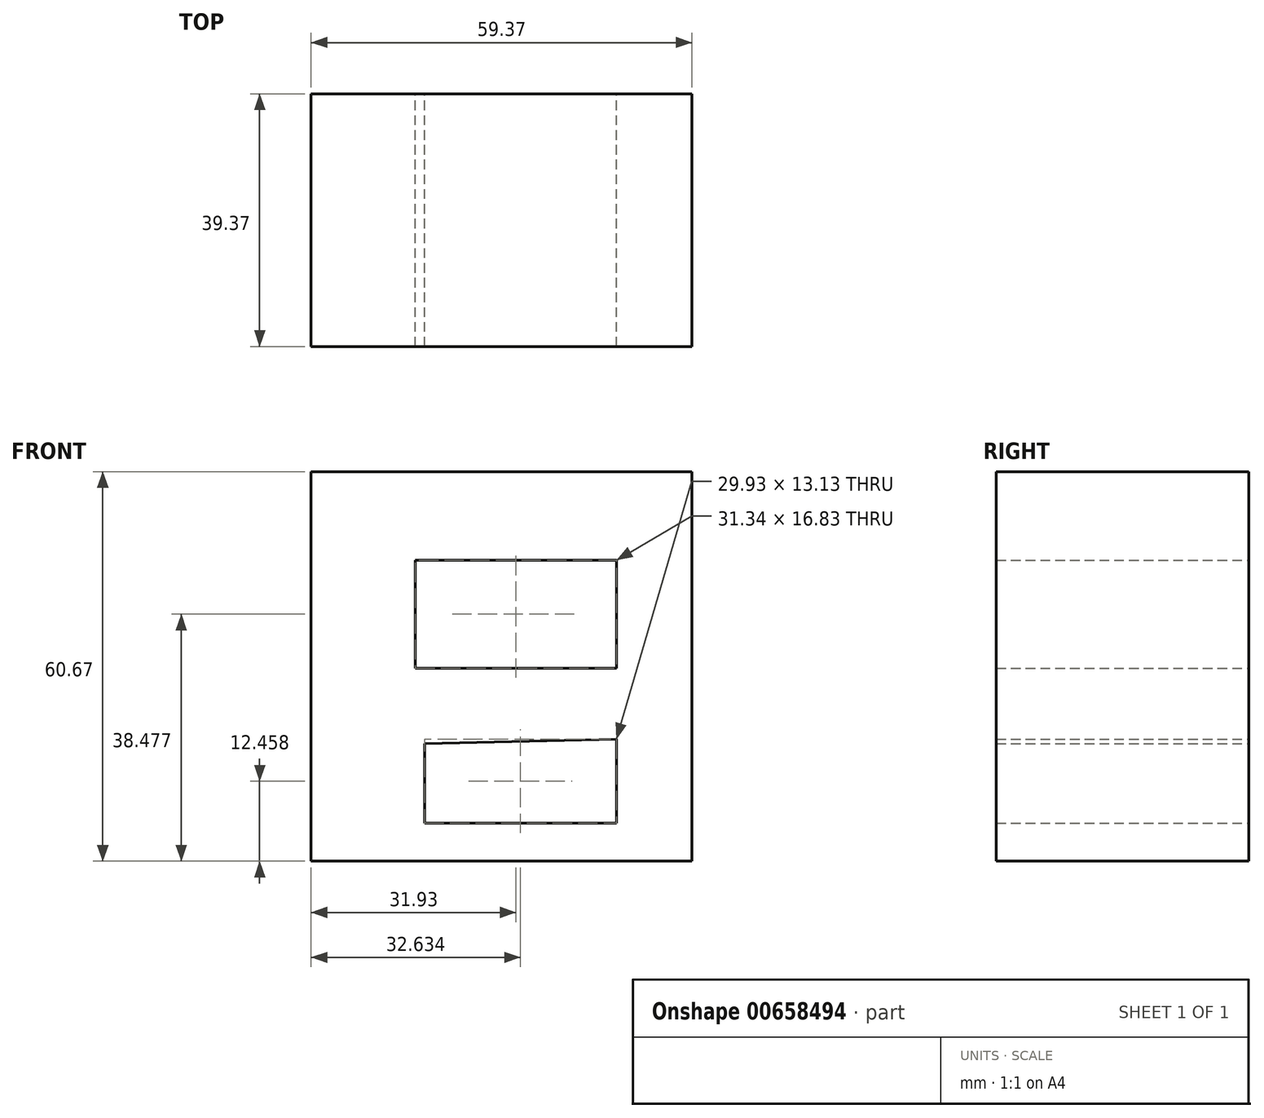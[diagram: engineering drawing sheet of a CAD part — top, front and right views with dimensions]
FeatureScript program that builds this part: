
annotation { "Feature Type Name" : "Feature", "Feature Type Description" : "" }
export const myFeature = defineFeature(function(context is Context, id is Id, definition is map)
    precondition{}
    {
        {
            var Q0;
            Q0=qCreatedBy(makeId("Front.planeOp"),FACE);
            var sketch = newSketch(context, id + "F0", { "sketchPlane" : qUnion([Q0])});
            skLineSegment(sketch, "E0", {"start": v(-28.67, 36.78) * mm, "end": v(30.7, 36.78) * mm});
            skLineSegment(sketch, "E1", {"start": v(30.7, 36.78) * mm, "end": v(30.7, -23.9) * mm});
            skLineSegment(sketch, "E2", {"start": v(30.7, -23.9) * mm, "end": v(-28.67, -23.9) * mm});
            skLineSegment(sketch, "E3", {"start": v(-28.67, -23.9) * mm, "end": v(-28.67, 36.78) * mm});
            skLineSegment(sketch, "E4", {"start": v(-12.41, 23) * mm, "end": v(18.93, 23) * mm});
            skLineSegment(sketch, "E5", {"start": v(18.93, 23) * mm, "end": v(18.93, 6.17) * mm});
            skLineSegment(sketch, "E6", {"start": v(18.93, 6.17) * mm, "end": v(-12.41, 6.17) * mm});
            skLineSegment(sketch, "E7", {"start": v(-12.41, 6.17) * mm, "end": v(-12.41, 23) * mm});
            skLineSegment(sketch, "E8", {"start": v(-11, -5.62) * mm, "end": v(-11, -18) * mm});
            skLineSegment(sketch, "E9", {"start": v(-11, -18) * mm, "end": v(18.93, -18) * mm});
            skLineSegment(sketch, "E10", {"start": v(18.93, -18) * mm, "end": v(18.93, -4.87) * mm});
            skLineSegment(sketch, "E11", {"start": v(18.93, -4.87) * mm, "end": v(-11, -5.62) * mm});
            skSolve(sketch);
        }
        {
            var Q0;
            Q0=makeQuery(id+"F0.imprint","IMPRINT",FACE,{"disambiguationData":[TD([[makeQuery(id+"F0.imprint","IMPRINT",EDGE,{"derivedFrom":sQuery(id+"F0.wireOp",EDGE,"E0")}),-1.0]])]});
            extrude(context, id + "F1", {"entities" : qUnion([Q0]), "depth" : 39.37 * mm, "offsetDistance" : 25.4 * mm});
        }
    });
